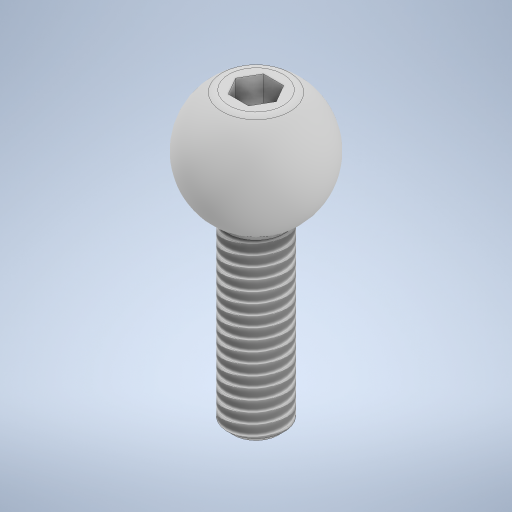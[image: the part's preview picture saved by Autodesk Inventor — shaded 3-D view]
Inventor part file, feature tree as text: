
AUTODESK INVENTOR PART (.ipt)
format: ipt  version: 2024 (Build 280153000, 153)  size: 319,488 bytes
history: native  units: in
note: dims shown in document units (in); Inventor stores cm internally (conversion verified against a paired STEP export)
features: sketch x3, fillet x2, plane x2, revolve x1, chamfer x1, split x1, extrude x1, thread x1, projected_geometry x1
ambient origin geometry x8: Origin, YZ Plane, XZ Plane, XY Plane, X Axis, Y Axis, Z Axis, Center Point
bodies: Solid1 (feature_tree)
feature tree (13):
  revolve  "Revolution1"  [1 undecoded]
  fillet  "Fillet1"  Radius=0.15in
  chamfer  "Chamfer1"  Distance=0.015in Angle=45.0deg
  sketch  "Sketch2"  dims[d3=360.0deg]
  plane  "Work Plane1"
  plane  "Work Plane2"
  split  "Split1"
  fillet  "Fillet2"  [1 undecoded]
  extrude  "Extrusion1"  Depth=0.032in
  thread  "Thread1"  [1 undecoded]
  sketch  "Sketch1"  dims[d0=0.325in d1=0.625in d2=0.15in]
  sketch  "Sketch3"  dims[d4=0.015in d5=0.015in d6=0.125in d7=45.0deg d9=0.0in d10=0.032in d11=0.0938in d12=0.1in d13=0.0in d14=0.457in d15=0.0in]
  projected_geometry  "Project Cut Edges1"
note: 3 required parameter values undecoded (feature->parameter linkage not recoverable at this tier; creation-order binding heuristic only, values carry confidence <= 0.55)